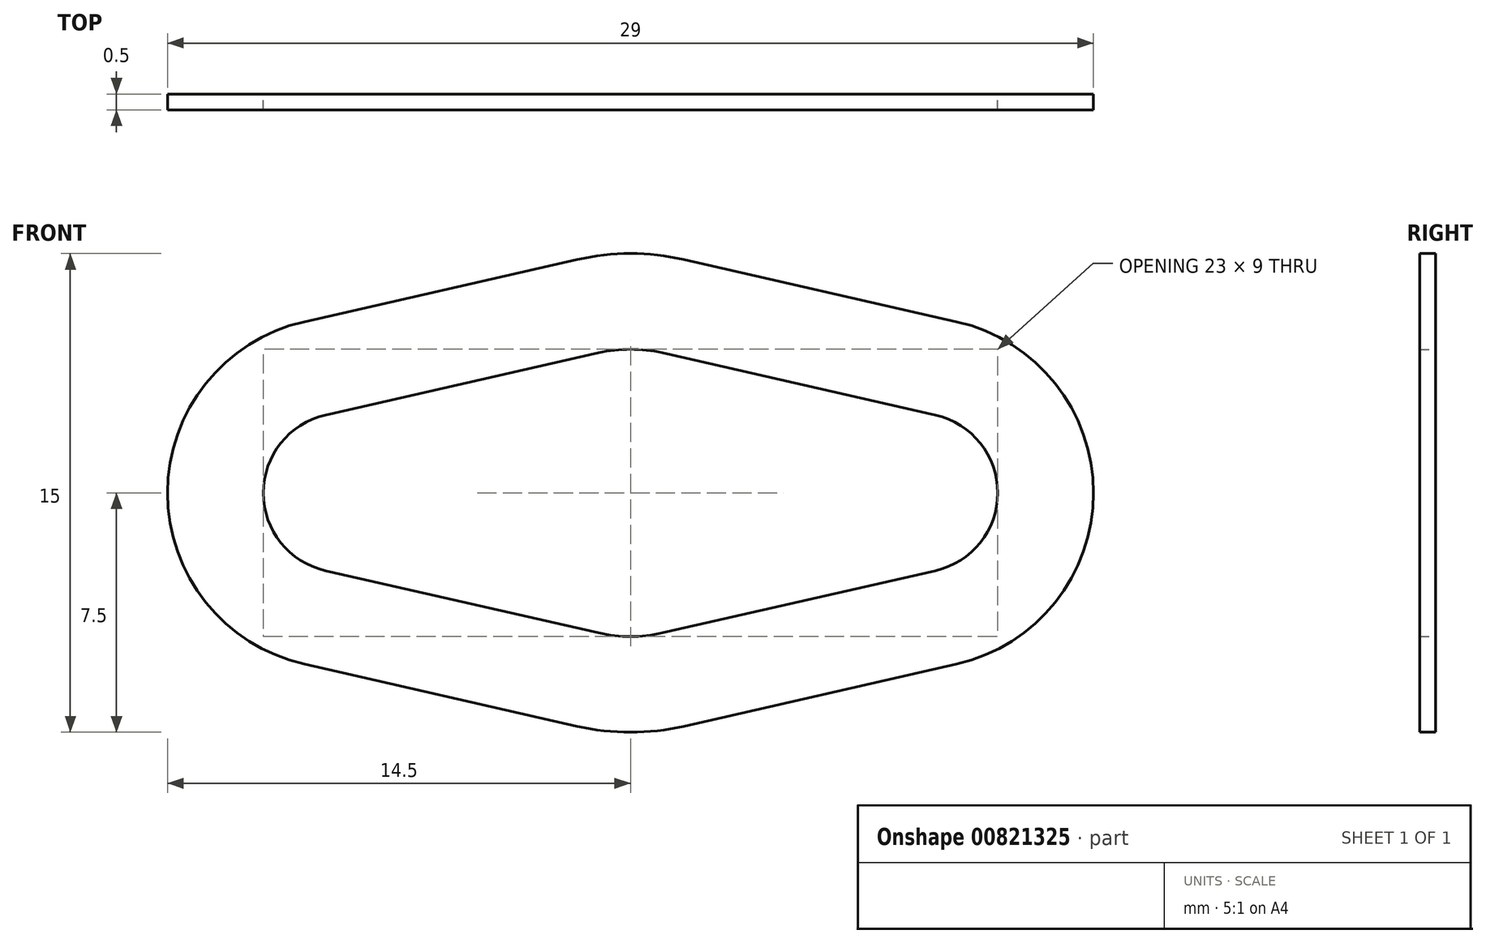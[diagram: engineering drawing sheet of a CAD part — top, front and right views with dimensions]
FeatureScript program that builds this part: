
annotation { "Feature Type Name" : "Feature", "Feature Type Description" : "" }
export const myFeature = defineFeature(function(context is Context, id is Id, definition is map)
    precondition{}
    {
        {
            var Q0;
            Q0=qCreatedBy(makeId("Front.planeOp"),FACE);
            var sketch = newSketch(context, id + "F0", { "sketchPlane" : qUnion([Q0])});
            skCircle(sketch, "E0", {"center": v(0, 0) * mm, "radius": 3.5 * mm, "construction": true});
            skCircle(sketch, "E1", {"center": v(9, 0) * mm, "radius": 1.5 * mm, "construction": true});
            skCircle(sketch, "E2", {"center": v(-9, 0) * mm, "radius": 1.5 * mm, "construction": true});
            skLineSegment(sketch, "E3", {"start": v(-9, 0) * mm, "end": v(0, 0) * mm, "construction": true});
            skLineSegment(sketch, "E4", {"start": v(0, 0) * mm, "end": v(9, 0) * mm, "construction": true});
            skArc(sketch, "E5.0", {"start": v(-9.56, 2.44) * mm, "mid": v(-11.5, 0) * mm, "end": v(-9.56, -2.44) * mm});
            skArc(sketch, "E6.0", {"start": v(9.56, -2.44) * mm, "mid": v(11.5, 0) * mm, "end": v(9.56, 2.44) * mm});
            skArc(sketch, "E7.0", {"start": v(-1, -4.39) * mm, "mid": v(0, -4.5) * mm, "end": v(1, -4.39) * mm});
            skLineSegment(sketch, "E8", {"start": v(-9.56, 2.44) * mm, "end": v(-1, 4.39) * mm});
            skLineSegment(sketch, "E9", {"start": v(1, 4.39) * mm, "end": v(9.56, 2.44) * mm});
            skLineSegment(sketch, "E10", {"start": v(-9.56, -2.44) * mm, "end": v(-1, -4.39) * mm});
            skLineSegment(sketch, "E11", {"start": v(1, -4.39) * mm, "end": v(9.56, -2.44) * mm});
            skArc(sketch, "E12.trimOffspring", {"start": v(1, 4.39) * mm, "mid": v(0, 4.5) * mm, "end": v(-1, 4.39) * mm});
            skArc(sketch, "E13.0", {"start": v(-10.22, 5.36) * mm, "mid": v(-14.5, 0) * mm, "end": v(-10.22, -5.36) * mm});
            skLineSegment(sketch, "E13.1", {"start": v(-10.22, -5.36) * mm, "end": v(-1.67, -7.31) * mm});
            skLineSegment(sketch, "E13.2", {"start": v(-10.22, 5.36) * mm, "end": v(-1.67, 7.31) * mm});
            skArc(sketch, "E13.3", {"start": v(-1.67, -7.31) * mm, "mid": v(0, -7.5) * mm, "end": v(1.67, -7.31) * mm});
            skArc(sketch, "E13.4", {"start": v(1.67, 7.31) * mm, "mid": v(0, 7.5) * mm, "end": v(-1.67, 7.31) * mm});
            skLineSegment(sketch, "E13.5", {"start": v(1.67, 7.31) * mm, "end": v(10.22, 5.36) * mm});
            skArc(sketch, "E13.6", {"start": v(10.22, -5.36) * mm, "mid": v(14.5, 0) * mm, "end": v(10.22, 5.36) * mm});
            skLineSegment(sketch, "E13.7", {"start": v(1.67, -7.31) * mm, "end": v(10.22, -5.36) * mm});
            skSolve(sketch);
        }
        {
            var Q0;
            Q0=makeQuery(id+"F0.imprint","IMPRINT",FACE,{"disambiguationData":[TD([[makeQuery(id+"F0.imprint","IMPRINT",EDGE,{"derivedFrom":sQuery(id+"F0.wireOp",EDGE,"E5.0")}),-1.0]])]});
            extrude(context, id + "F1", {"entities" : qUnion([Q0]), "depth" : .5 * mm, "offsetDistance" : 25 * mm});
        }
    });
